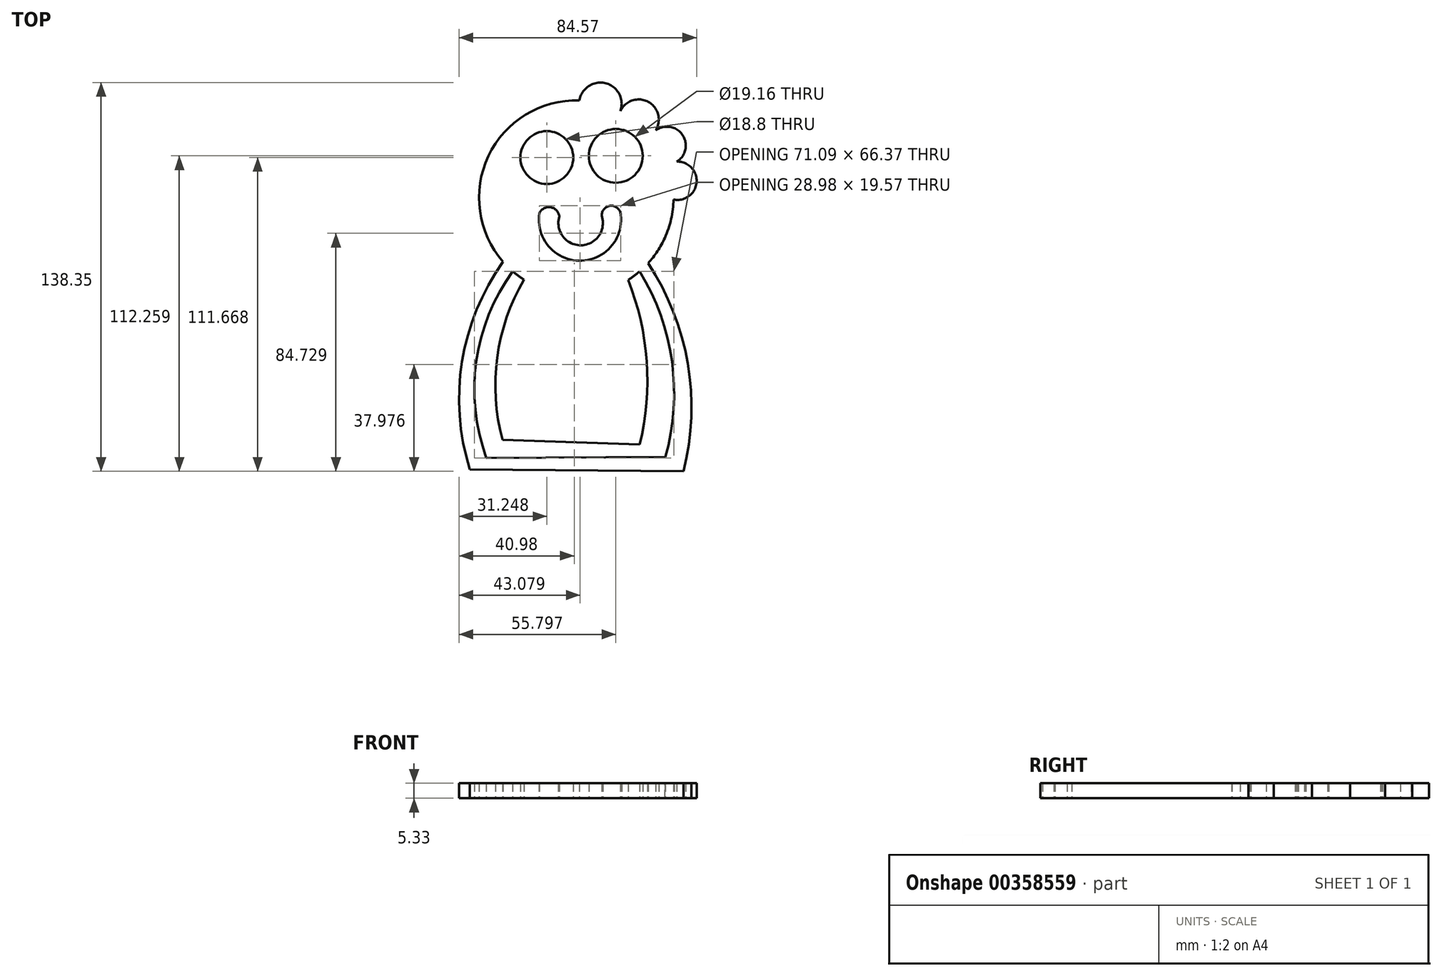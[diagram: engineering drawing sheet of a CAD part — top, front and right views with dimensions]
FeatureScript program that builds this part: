
annotation { "Feature Type Name" : "Feature", "Feature Type Description" : "" }
export const myFeature = defineFeature(function(context is Context, id is Id, definition is map)
    precondition{}
    {
        {
            var Q0;
            Q0=qCreatedBy(makeId("Top.planeOp"),FACE);
            var sketch = newSketch(context, id + "F0", { "sketchPlane" : qUnion([Q0])});
            skCircle(sketch, "E0", {"center": v(-38.15, 26.2) * mm, "radius": 34.6 * mm});
            skArc(sketch, "E1", {"start": v(-22.44, 57.04) * mm, "mid": v(-27.67, 66.95) * mm, "end": v(-37.03, 60.8) * mm});
            skArc(sketch, "E2", {"start": v(-11.56, 48.35) * mm, "mid": v(-11.47, 59.63) * mm, "end": v(-22.44, 57.04) * mm});
            skArc(sketch, "E3", {"start": v(-5.65, 38.1) * mm, "mid": v(-0.05, 48.14) * mm, "end": v(-11.56, 48.35) * mm});
            skArc(sketch, "E4", {"start": v(-3.55, 25.6) * mm, "mid": v(4.61, 33.4) * mm, "end": v(-5.65, 38.1) * mm});
            skArc(sketch, "E5", {"start": v(-1.89, 25.45) * mm, "mid": v(-2.72, 25.57) * mm, "end": v(-3.55, 25.6) * mm});
            skCircle(sketch, "E6", {"center": v(-48.61, 40.5) * mm, "radius": 9.4 * mm});
            skCircle(sketch, "E7", {"center": v(-24.06, 41.1) * mm, "radius": 9.58 * mm});
            skArc(sketch, "E8", {"start": v(-51.27, 20.7) * mm, "mid": v(-37.12, 3.78) * mm, "end": v(-22.29, 20.1) * mm});
            skArc(sketch, "E9", {"start": v(-44.18, 19.5) * mm, "mid": v(-36.43, 9.3) * mm, "end": v(-29.1, 19.8) * mm});
            skArc(sketch, "E10", {"start": v(-44.18, 19.5) * mm, "mid": v(-47.27, 22.82) * mm, "end": v(-51.27, 20.7) * mm});
            skArc(sketch, "E11", {"start": v(-22.29, 20.1) * mm, "mid": v(-25.84, 23.35) * mm, "end": v(-29.1, 19.8) * mm});
            skPoint(sketch, "E12.first.point", {"position": v(-47.69, -7.05) * mm});
            skPoint(sketch, "E12.second.point", {"position": v(-64.41, -59.96) * mm});
            skPoint(sketch, "E12.third.point", {"position": v(-6.39, -49.94) * mm});
            skPoint(sketch, "E13.first.point", {"position": v(-154.17, -9.45) * mm});
            skPoint(sketch, "E13.second.point", {"position": v(-151.25, -4.02) * mm});
            skPoint(sketch, "E13.third.point", {"position": v(-150.83, 0) * mm});
            skPoint(sketch, "E14.1.internal.orphan", {"position": v(0, -49.94) * mm});
            skPoint(sketch, "E14.2.internal.orphan", {"position": v(5.08, -49.94) * mm});
            skPoint(sketch, "E15.endSnap0", {"position": v(3.67, 16.8) * mm});
            skPoint(sketch, "E16.start.orphan", {"position": v(-81.94, 0) * mm});
            skPoint(sketch, "E17.end.orphan", {"position": v(3.67, 4.25) * mm});
            skPoint(sketch, "E17.start.orphan", {"position": v(7.29, 0) * mm});
            skArc(sketch, "E18", {"start": v(-15.57, -61.57) * mm, "mid": v(-13.07, -32) * mm, "end": v(-19.7, -3.06) * mm});
            skArc(sketch, "E19", {"start": v(-56.75, -2.97) * mm, "mid": v(-66.28, -30.7) * mm, "end": v(-64.41, -59.96) * mm});
            skLineSegment(sketch, "E20", {"start": v(-64.41, -59.96) * mm, "end": v(-15.57, -61.57) * mm});
            skArc(sketch, "E21", {"start": v(-6.39, -66) * mm, "mid": v(-4.08, -32.04) * mm, "end": v(-15.56, 0) * mm});
            skArc(sketch, "E22", {"start": v(-60.74, 0) * mm, "mid": v(-73.73, -32) * mm, "end": v(-70.14, -66.37) * mm});
            skLineSegment(sketch, "E23", {"start": v(-70.14, -66.37) * mm, "end": v(-6.39, -66) * mm});
            skArc(sketch, "E24", {"start": v(0, -71.16) * mm, "mid": v(1.54, -32.8) * mm, "end": v(-12.56, 2.92) * mm});
            skArc(sketch, "E25", {"start": v(-64.16, 3.4) * mm, "mid": v(-78.8, -32.12) * mm, "end": v(-76.04, -70.42) * mm});
            skLineSegment(sketch, "E26", {"start": v(-76.04, -70.42) * mm, "end": v(0, -71.16) * mm});
            skFitSpline(sketch, "E27", {"points": [v(-6.62, 11.95) * mm, v(-6.62, 11.95) * mm], "startDerivative": vector(-0.01, 0) * mm, "endDerivative": vector(-0.01, 0) * mm});
            skFitSpline(sketch, "E28", {"points": [v(-6.62, 11.95) * mm, v(-6.62, 11.95) * mm], "startDerivative": vector(-0.01, 0) * mm, "endDerivative": vector(-0.01, 0) * mm});
            skPoint(sketch, "E29.2.internal.orphan", {"position": v(-6.62, 11.9) * mm});
            skPoint(sketch, "E30.startDerivative.orphan", {"position": v(-6.62, 11.94) * mm});
            skSolve(sketch);
        }
        {
            var Q0;
            Q0 = qSketchRegion(id + "F0", true);
            var Q1;
            {var subQ0=sQuery(id+"F0.wireOp",EDGE,"E18");Q1=makeQuery(id+"F0.imprint","IMPRINT",FACE,{"disambiguationData":[TD([[makeQuery(id+"F0.imprint","IMPRINT",EDGE,{"derivedFrom":subQ0}),1.0]])]});}
            extrude(context, id + "F1", {"entities" : qUnion([Q0, Q1]), "depth" : 5.33 * mm});
        }
    });
